# Revit family: Lustro_uchylne_dla_niepełnosprawnych z uchwytem-700 x 500 mm
name_source: partatom
category: Furniture
units: mm (PartAtom-declared; Revit-internal decimal feet)

## family parameters
Always vertical = Yes
Cut with Voids When Loaded = No
Host = Wall
Room Calculation Point = No
Shared = No

## types (1)
- N08023S
    Depth / Glebokosc = 75 mm  [stored 0.246063 ft]
    Description = Lustro uchylne dla niepełnosprawnych z uchwytem 700 x 500 mm to bardzo ważny element wyposażenia toalet ogólnodostępnych, odwiedzanych także przez osoby z dysfunkcjami ruchowymi. Dzięki uchwytowi użytkownik może dostosować kąt nachylenia lustra do własnych potrzeb, co zwiększa jego komfort i wygodę. Lustro uchylne wykonane jest z laminowanego szkła, a wykończone stalową, odporną na uszkodzenia ramą. Pasuje idealnie do nowoczesnych obiektów typu hotele, czy centra handlowe. Swoją funkcjonalnością zaspokaja potrzeby nawet najbardziej wymagających użytkowników.
    Height / Wysokosc = 700 mm  [stored 2.29659 ft]
    Lustro = Lustro
    Manufacturer = FANECO.com
    Manufacturer code / Kod producenta = 5901764293415
    Material finish / Wykonczenie = Materiał Stal nierdzewna AISI 304 (rama, blacha), laminowane szkło (lustro)
    Material ramy = Stal nierdzewna AISI 304
    Product code / Kod produktu = N08023S
    URL = https://faneco.com
    Weight / Waga = 3.2 kg
    Width / Szerokosc = 500 mm  [stored 1.64042 ft]

note: [stored X ft] marks values corroborated as IEEE doubles in the binary element streams (Revit-internal decimal feet)

## geometry (parser evidence)
native form markers: Sweep x11
no freeform markers — native parametric forms only
